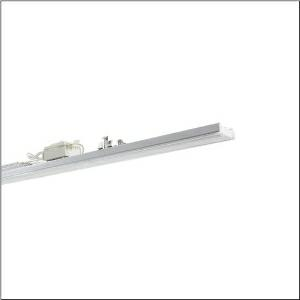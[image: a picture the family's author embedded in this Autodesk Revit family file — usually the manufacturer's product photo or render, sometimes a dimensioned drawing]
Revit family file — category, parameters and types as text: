
# Revit family: licross_r__21_recessed_mo_52te1edn495g_06d0
name_source: partatom
category: Lighting Fixtures
units: mm (PartAtom-declared; Revit-internal decimal feet)

## family parameters
Cut with Voids When Loaded = No
Host = Face
Light Source = No
Part Type = Normal
Room Calculation Point = No
Round Connector Dimension = Use Diameter
Shared = No

## types (1)
- --- (1 x LED, 9940 lm, 58 W, 4000K)
    Apparent Load = 58 VA
    CIE Flux Codes = 85 95 99 100 100
    Color Rendering = 80
    Color Temperature = 4000K
    Default Elevation = 1800 mm
    Description = Licross® 21 Recessed MO, luminaire insert, of sheet steel, galvanised, coil coated, white, length: 1.500mm, width: 66mm, height: 67mm, LED rated luminous flux: 9.940lm, light colour: 840, control gear: DALI 2, with plug, 5-pole, with phase selection, mains connection: 220..240V, AC, 50/60Hz, rated input power: 58W, halogen-free wiring, primary light control with lens, of plastic, primary optical cover: cover, of PMMA, light emission: direct distribution, primary light characteristic: symmetric, protection rating (complete): IP54, insulation class (complete): insulation class I (protective earthing), certification: CE, ENEC, VDE, UKCA, protection symbol: D if used in an environment with non-conductive dust loads with corresponding accessories, impact resistance: IK06, permissible ambient temperature for indoor applications: -25..+35°C, corresponds to IFS (International Featured Standards) requirements for safety and quality in the food industry, reducing of maximum allowable ambient temperature of 5°C with ceiling mounting, LABS conformity tested according to VDMA 24364:2018-05, packaging unit: 1 piece
    Height = 58 mm
    Lamp = 1 x LED
    Lamp Light Flux = 9940 lm
    Lamp Power = 58 W
    Lamp count = 1
    Length = 1500 mm
    Luminous efficacy = 171 lm/W
    Manufacturer = Siteco
    ModVariant = No
    Model = 52TE1EDN495G
    Mounting Place = Ceiling
    Mounting Type = Pendant
    Number of Poles = 1
    OnlyDefault = Yes
    Power Factor = 1
    Product Name = Licross® 21 Recessed MO
    Product group = luminaire insert
    ProductGroupID = 902
    Protection Class = Protection class I
    Protection Degree = IP 54
    RLX_Detail_Level = 1
    RLX_Emergency_Light_Flux = 0 lm
    RLX_Emergency_Type = 0
    RLX_Emergency_Type_DB = No
    RlxData = <blob elided: 24633 chars, md5=64d25b97>
    Socket = socket
    Standby Power = 0 W
    System Light Flux = 9940 lm
    System Power = 58 W
    Type Comments = factory setting: luminous flux: 100 % | dim-lin: 254 | 390 mA
    Type Image = l_1296930.jpg
    URL = http://relux.com
    VarID = @adj_125012
    Voltage = 0 V
    Weight = 0.00 kg
    Width = 66 mm

## geometry (parser evidence)
native form markers: Blend x4, Sweep x11
no freeform markers — native parametric forms only
